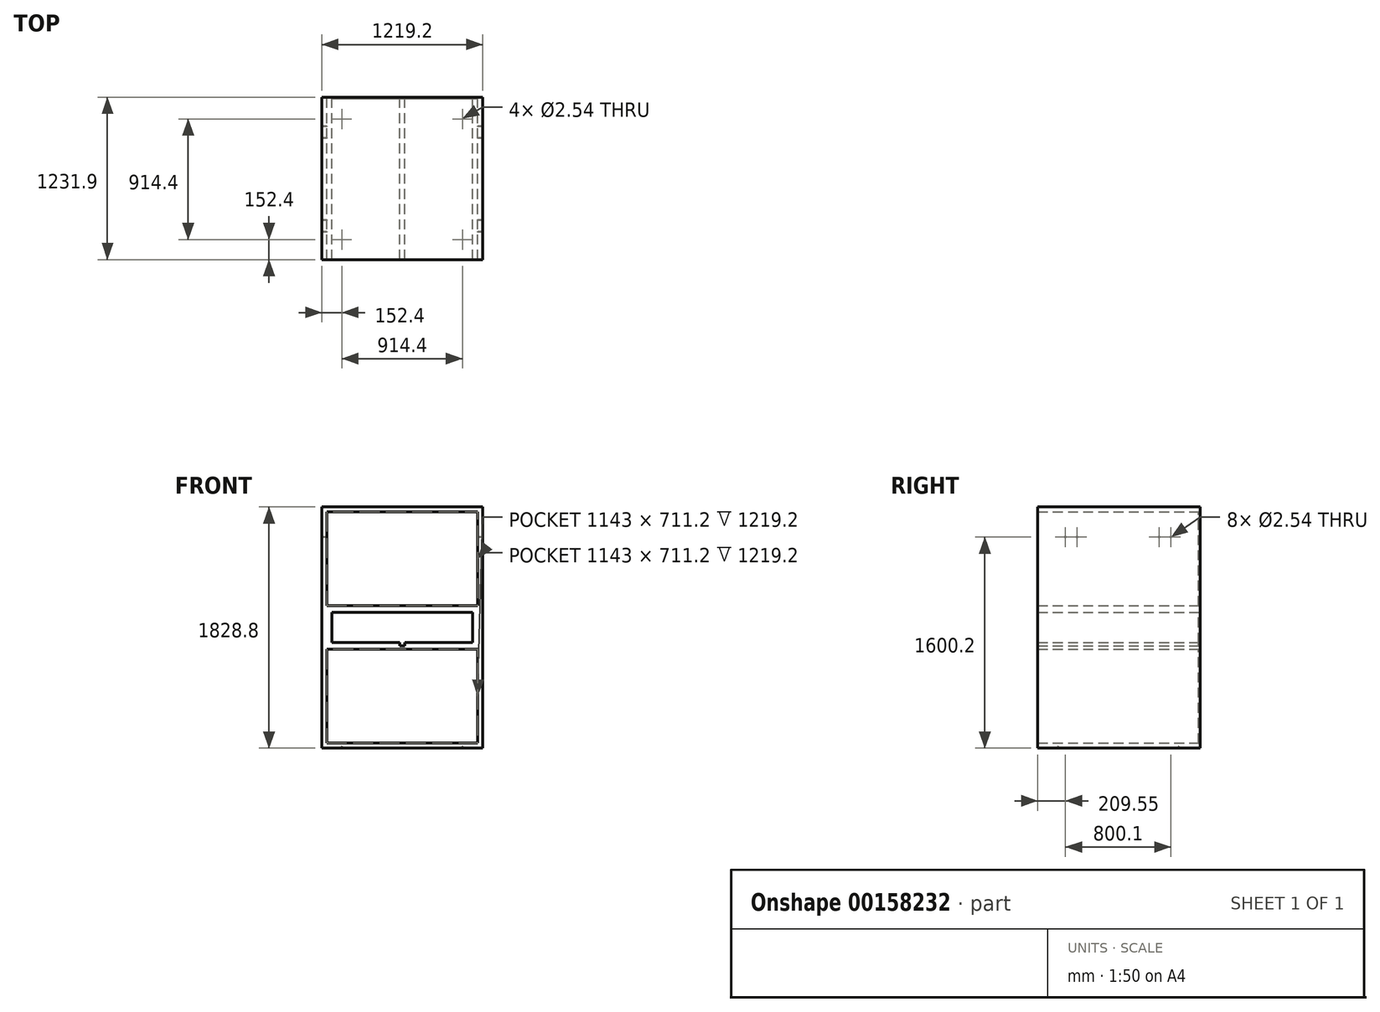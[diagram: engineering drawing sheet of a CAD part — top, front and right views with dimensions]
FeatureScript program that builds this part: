
annotation { "Feature Type Name" : "Feature", "Feature Type Description" : "" }
export const myFeature = defineFeature(function(context is Context, id is Id, definition is map)
    precondition{}
    {
        {
            var Q0;
            Q0=qCreatedBy(makeId("Front.planeOp"),FACE);
            var sketch = newSketch(context, id + "F0", { "sketchPlane" : qUnion([Q0])});
            skLineSegment(sketch, "E0.bottom", {"start": v(609.6, -914.4) * mm, "end": v(-609.6, -914.4) * mm});
            skLineSegment(sketch, "E0.top", {"start": v(609.6, 914.4) * mm, "end": v(-609.6, 914.4) * mm});
            skLineSegment(sketch, "E0.left", {"start": v(609.6, -914.4) * mm, "end": v(609.6, 914.4) * mm});
            skLineSegment(sketch, "E0.right", {"start": v(-609.6, -914.4) * mm, "end": v(-609.6, 914.4) * mm});
            skPoint(sketch, "E0.middle", {"position": v(0, 0) * mm});
            skLineSegment(sketch, "E1.0", {"start": v(571.5, 876.3) * mm, "end": v(-571.5, 876.3) * mm});
            skLineSegment(sketch, "E1.1", {"start": v(571.5, -876.3) * mm, "end": v(571.5, -165.1) * mm});
            skLineSegment(sketch, "E1.2", {"start": v(571.5, -876.3) * mm, "end": v(-571.5, -876.3) * mm});
            skLineSegment(sketch, "E1.3", {"start": v(-571.5, -876.3) * mm, "end": v(-571.5, -165.1) * mm});
            skLineSegment(sketch, "E2", {"start": v(-571.5, 165.1) * mm, "end": v(571.5, 165.1) * mm});
            skLineSegment(sketch, "E3", {"start": v(-571.5, -165.1) * mm, "end": v(571.5, -165.1) * mm});
            skLineSegment(sketch, "E4.bottom", {"start": v(533.4, -114.3) * mm, "end": v(-533.4, -114.3) * mm});
            skLineSegment(sketch, "E4.top", {"start": v(533.4, 114.3) * mm, "end": v(-533.4, 114.3) * mm});
            skLineSegment(sketch, "E4.left", {"start": v(533.4, -114.3) * mm, "end": v(533.4, 114.3) * mm});
            skLineSegment(sketch, "E4.right", {"start": v(-533.4, -114.3) * mm, "end": v(-533.4, 114.3) * mm});
            skLineSegment(sketch, "E5.trimOffspring", {"start": v(-571.5, 165.1) * mm, "end": v(-571.5, 876.3) * mm});
            skLineSegment(sketch, "E6.trimOffspring", {"start": v(571.5, 165.1) * mm, "end": v(571.5, 876.3) * mm});
            skSolve(sketch);
        }
        {
            var Q0;
            Q0 = qSketchRegion(id + "F0", true);
            var Q1;
            Q1=makeQuery(id+"F0.imprint","IMPRINT",FACE,{"disambiguationData":[TD([[makeQuery(id+"F0.imprint","IMPRINT",EDGE,{"derivedFrom":sQuery(id+"F0.wireOp",EDGE,"iGZaj2ei-qv5i-Wc05-VPX8-QgNIyJMI4kAF.bottom")}),1.0]])]});
            extrude(context, id + "F1", {"entities" : qUnion([Q0, Q1]), "endBound" : BoundingType.SYMMETRIC, "depth" : 1219.2 * mm});
        }
        {
            var Q0;
            Q0=makeQuery(id+"F1.opExtrude","CAP_FACE",FACE,{"disambiguationData":[OSD([sQuery(id+"F0.wireOp",EDGE,"E0.bottom"),sQuery(id+"F0.wireOp",EDGE,"E0.top"),sQuery(id+"F0.wireOp",EDGE,"E0.left"),sQuery(id+"F0.wireOp",EDGE,"E0.right"),sQuery(id+"F0.wireOp",EDGE,"E1.0"),sQuery(id+"F0.wireOp",EDGE,"E1.1"),sQuery(id+"F0.wireOp",EDGE,"E1.2"),sQuery(id+"F0.wireOp",EDGE,"E1.3"),sQuery(id+"F0.wireOp",EDGE,"E2"),sQuery(id+"F0.wireOp",EDGE,"E3"),sQuery(id+"F0.wireOp",EDGE,"E4.bottom"),sQuery(id+"F0.wireOp",EDGE,"E4.top"),sQuery(id+"F0.wireOp",EDGE,"E4.left"),sQuery(id+"F0.wireOp",EDGE,"E4.right"),sQuery(id+"F0.wireOp",EDGE,"E5.trimOffspring"),sQuery(id+"F0.wireOp",EDGE,"E6.trimOffspring")])],"isStart":true});
            var sketch = newSketch(context, id + "F2", { "sketchPlane" : qUnion([Q0])});
            skLineSegment(sketch, "E7.bottom", {"start": v(609.6, -914.4) * mm, "end": v(-609.6, -914.4) * mm});
            skLineSegment(sketch, "E7.top", {"start": v(609.6, 914.4) * mm, "end": v(-609.6, 914.4) * mm});
            skLineSegment(sketch, "E7.left", {"start": v(609.6, -914.4) * mm, "end": v(609.6, 914.4) * mm});
            skLineSegment(sketch, "E7.right", {"start": v(-609.6, -914.4) * mm, "end": v(-609.6, 914.4) * mm});
            skPoint(sketch, "E7.middle", {"position": v(0, 0) * mm});
            skSolve(sketch);
        }
        {
            var Q0;
            Q0 = qSketchRegion(id + "F2", true);
            extrude(context, id + "F3", {"entities" : qUnion([Q0]), "operationType" : NewBodyOperationType.ADD, "depth" : 12.7 * mm});
        }
        {
            var Q0;
            Q0=makeQuery(id+"F3.boolean.opBoolean","MERGE",FACE,{"derivedFrom":[makeQuery(id+"F1.opExtrude","SWEPT_FACE",FACE,{"disambiguationData":[OSD([sQuery(id+"F0.wireOp",EDGE,"E0.right")])]}),makeQuery(id+"F3.opExtrude","SWEPT_FACE",FACE,{"disambiguationData":[OSD([sQuery(id+"F2.wireOp",EDGE,"E7.left")])]})]});
            var sketch = newSketch(context, id + "F4", { "sketchPlane" : qUnion([Q0])});
            skPoint(sketch, "E8", {"position": v(-400.05, 685.8) * mm});
            skPoint(sketch, "E9", {"position": v(-311.15, 685.8) * mm});
            skPoint(sketch, "E10.MirrorP", {"position": v(311.15, 685.8) * mm});
            skPoint(sketch, "E11.MirrorP", {"position": v(400.05, 685.8) * mm});
            skSolve(sketch);
        }
        {
            var Q0;
            Q0=sQuery(id+"F4.wireOp",VERTEX,"E8");
            var Q1;
            Q1=sQuery(id+"F4.wireOp",VERTEX,"E9");
            var Q2;
            Q2=sQuery(id+"F4.wireOp",VERTEX,"E10.MirrorP");
            var Q3;
            Q3=sQuery(id+"F4.wireOp",VERTEX,"E11.MirrorP");
            var Q4;
            Q4=makeQuery(id+"F1.opExtrude","SWEPT_BODY",BODY,{"disambiguationData":[OSD([sQuery(id+"F0.wireOp",EDGE,"E0.bottom"),sQuery(id+"F0.wireOp",EDGE,"E0.top"),sQuery(id+"F0.wireOp",EDGE,"E0.left"),sQuery(id+"F0.wireOp",EDGE,"E0.right"),sQuery(id+"F0.wireOp",EDGE,"E1.0"),sQuery(id+"F0.wireOp",EDGE,"E1.1"),sQuery(id+"F0.wireOp",EDGE,"E1.2"),sQuery(id+"F0.wireOp",EDGE,"E1.3"),sQuery(id+"F0.wireOp",EDGE,"E2"),sQuery(id+"F0.wireOp",EDGE,"E3"),sQuery(id+"F0.wireOp",EDGE,"E4.bottom"),sQuery(id+"F0.wireOp",EDGE,"E4.top"),sQuery(id+"F0.wireOp",EDGE,"E4.left"),sQuery(id+"F0.wireOp",EDGE,"E4.right"),sQuery(id+"F0.wireOp",EDGE,"E5.trimOffspring"),sQuery(id+"F0.wireOp",EDGE,"E6.trimOffspring")])]});
            hole(context, id + "F5", {"style" : HoleStyle.SIMPLE, "endStyle" : HoleEndStyle.THROUGH, "holeDiameter" : 2.54 * mm, "locations" : qUnion([Q0, Q1, Q2, Q3]), "scope" : qUnion([Q4]), "isTappedThrough" : true});
        }
        {
            var Q0;
            Q0=makeQuery(id+"F3.boolean.opBoolean","MERGE",FACE,{"derivedFrom":[makeQuery(id+"F1.opExtrude","SWEPT_FACE",FACE,{"disambiguationData":[OSD([sQuery(id+"F0.wireOp",EDGE,"E0.bottom")])]}),makeQuery(id+"F3.opExtrude","SWEPT_FACE",FACE,{"disambiguationData":[OSD([sQuery(id+"F2.wireOp",EDGE,"E7.bottom")])]})]});
            var sketch = newSketch(context, id + "F6", { "sketchPlane" : qUnion([Q0])});
            skPoint(sketch, "E12", {"position": v(-457.2, 457.2) * mm});
            skPoint(sketch, "E13.MirrorP", {"position": v(457.2, 457.2) * mm});
            skPoint(sketch, "E14.MirrorP", {"position": v(-457.2, -457.2) * mm});
            skPoint(sketch, "E15.MirrorP", {"position": v(457.2, -457.2) * mm});
            skSolve(sketch);
        }
        {
            var Q0;
            Q0=sQuery(id+"F6.wireOp",VERTEX,"E12");
            var Q1;
            Q1=sQuery(id+"F6.wireOp",VERTEX,"E13.MirrorP");
            var Q2;
            Q2=sQuery(id+"F6.wireOp",VERTEX,"E15.MirrorP");
            var Q3;
            Q3=sQuery(id+"F6.wireOp",VERTEX,"E14.MirrorP");
            var Q4;
            Q4=makeQuery(id+"F1.opExtrude","SWEPT_BODY",BODY,{"disambiguationData":[OSD([sQuery(id+"F0.wireOp",EDGE,"E0.bottom"),sQuery(id+"F0.wireOp",EDGE,"E0.top"),sQuery(id+"F0.wireOp",EDGE,"E0.left"),sQuery(id+"F0.wireOp",EDGE,"E0.right"),sQuery(id+"F0.wireOp",EDGE,"E1.0"),sQuery(id+"F0.wireOp",EDGE,"E1.1"),sQuery(id+"F0.wireOp",EDGE,"E1.2"),sQuery(id+"F0.wireOp",EDGE,"E1.3"),sQuery(id+"F0.wireOp",EDGE,"E2"),sQuery(id+"F0.wireOp",EDGE,"E3"),sQuery(id+"F0.wireOp",EDGE,"E4.bottom"),sQuery(id+"F0.wireOp",EDGE,"E4.top"),sQuery(id+"F0.wireOp",EDGE,"E4.left"),sQuery(id+"F0.wireOp",EDGE,"E4.right"),sQuery(id+"F0.wireOp",EDGE,"E5.trimOffspring"),sQuery(id+"F0.wireOp",EDGE,"E6.trimOffspring")])]});
            hole(context, id + "F7", {"style" : HoleStyle.SIMPLE, "endStyle" : HoleEndStyle.BLIND, "holeDiameter" : 2.54 * mm, "holeDepth" : 12.7 * mm, "locations" : qUnion([Q0, Q1, Q2, Q3]), "scope" : qUnion([Q4])});
        }
        {
            var Q0;
            Q0=makeQuery(id+"F1.opExtrude","SWEPT_FACE",FACE,{"disambiguationData":[OSD([sQuery(id+"F0.wireOp",EDGE,"E4.bottom")])]});
            var sketch = newSketch(context, id + "F8", { "sketchPlane" : qUnion([Q0])});
            skLineSegment(sketch, "E16.bottom", {"start": v(19.05, -609.6) * mm, "end": v(-19.05, -609.6) * mm});
            skLineSegment(sketch, "E16.top", {"start": v(19.05, 609.6) * mm, "end": v(-19.05, 609.6) * mm});
            skPoint(sketch, "E16.middle", {"position": v(0, 0) * mm});
            skLineSegment(sketch, "E17", {"start": v(19.05, -609.6) * mm, "end": v(19.05, 609.6) * mm});
            skLineSegment(sketch, "E18", {"start": v(-19.05, -609.6) * mm, "end": v(-19.05, 609.6) * mm});
            skSolve(sketch);
        }
        {
            var Q0;
            Q0 = qSketchRegion(id + "F8", true);
            extrude(context, id + "F9", {"entities" : qUnion([Q0]), "operationType" : NewBodyOperationType.REMOVE, "oppositeDirection" : true, "depth" : 25.4 * mm});
        }
    });
